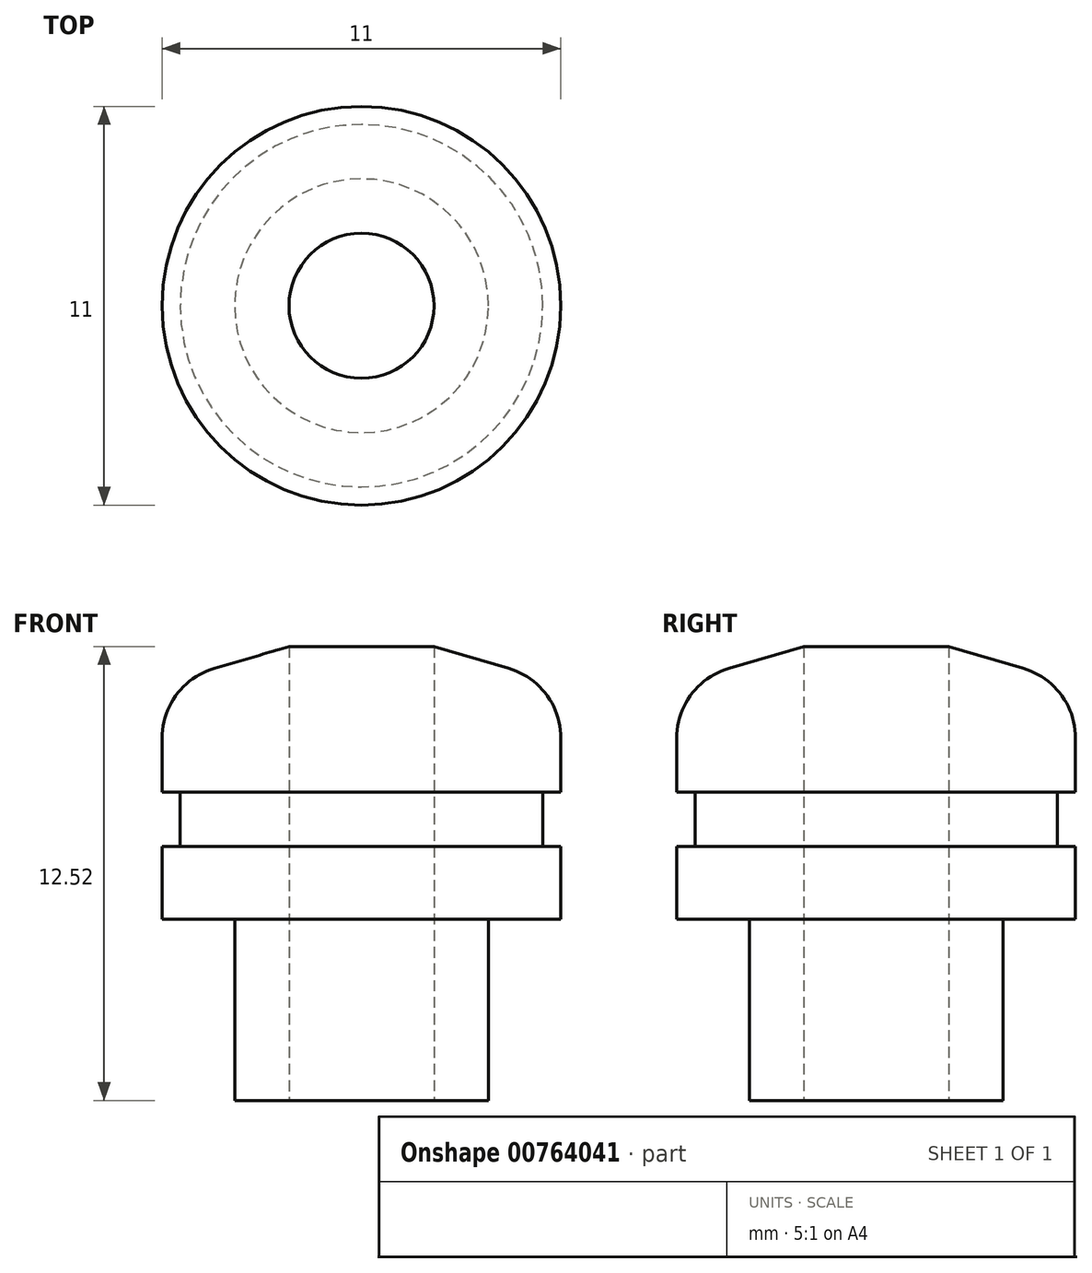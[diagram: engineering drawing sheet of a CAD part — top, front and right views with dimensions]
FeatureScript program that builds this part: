
annotation { "Feature Type Name" : "Feature", "Feature Type Description" : "" }
export const myFeature = defineFeature(function(context is Context, id is Id, definition is map)
    precondition{}
    {
        {
            var Q0;
            Q0=qCreatedBy(makeId("Front.planeOp"),FACE);
            var sketch = newSketch(context, id + "F0", { "sketchPlane" : qUnion([Q0])});
            skLineSegment(sketch, "E0", {"start": v(0, 0) * mm, "end": v(0, 10.48) * mm, "construction": true});
            skLineSegment(sketch, "E1", {"start": v(2, 12.52) * mm, "end": v(2, 0) * mm});
            skLineSegment(sketch, "E2", {"start": v(2, 0) * mm, "end": v(3.5, 0) * mm});
            skLineSegment(sketch, "E3", {"start": v(3.5, 0) * mm, "end": v(3.5, 5) * mm});
            skLineSegment(sketch, "E4", {"start": v(3.5, 5) * mm, "end": v(5.5, 5) * mm});
            skLineSegment(sketch, "E5", {"start": v(5.5, 5) * mm, "end": v(5.5, 7) * mm});
            skLineSegment(sketch, "E6", {"start": v(5.5, 7) * mm, "end": v(5, 7) * mm});
            skLineSegment(sketch, "E7", {"start": v(5, 7) * mm, "end": v(5, 8.5) * mm});
            skLineSegment(sketch, "E8", {"start": v(5, 8.5) * mm, "end": v(5.5, 8.5) * mm});
            skLineSegment(sketch, "E9", {"start": v(5.5, 8.5) * mm, "end": v(5.5, 11.5) * mm});
            skLineSegment(sketch, "E10", {"start": v(5.5, 11.5) * mm, "end": v(2, 12.52) * mm});
            skSolve(sketch);
        }
        {
            var Q0;
            Q0 = qSketchRegion(id + "F0", true);
            var Q1;
            Q1=sQuery(id+"F0.wireOp",EDGE,"E0");
            revolve(context, id + "F1", {"surfaceOperationType" : NewSurfaceOperationType.NEW, "entities" : qUnion([Q0]), "axis" : qUnion([Q1]), "revolveType" : RevolveType.FULL});
        }
        {
            var Q0;
            Q0=makeQuery(id+"F1.opRevolve","SWEPT_EDGE",EDGE,{"disambiguationData":[OSD([sQuery(id+"F0.wireOp",EDGE,"E9"),sQuery(id+"F0.wireOp",EDGE,"E10")])]});
            fillet(context, id + "F2", {"entities" : qUnion([Q0]), "radius" : 2 * mm, "tangentPropagation" : true, "allowEdgeOverflow" : false});
        }
    });
